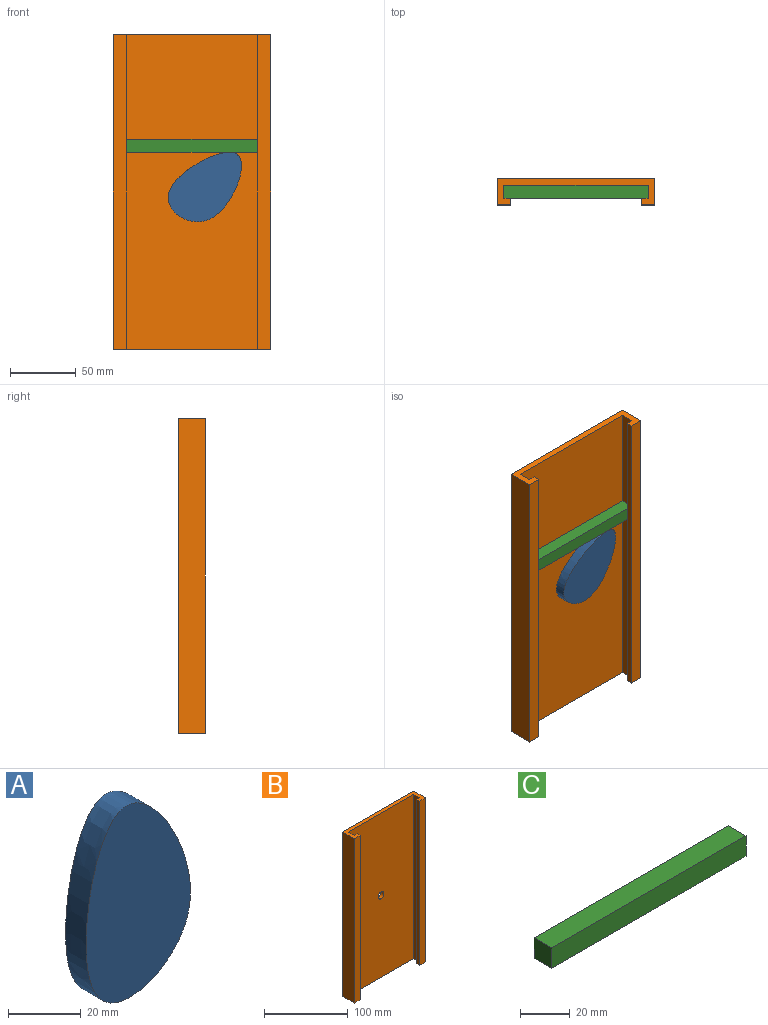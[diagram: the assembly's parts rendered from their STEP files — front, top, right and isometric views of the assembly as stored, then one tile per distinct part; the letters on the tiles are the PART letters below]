
ASSEMBLY  parts=3 mates=2
PART A: 5 faces, bbox 45.8x15x68.5 mm
  f0: plane 10x10mm, normal (0,1,0), area 78.5mm2, adj f1
  f1: cylinder r=5mm len=10mm, axis (0,-1,0), area 219.9mm2, adj f0,f4
  f2: extruded ~65.05x40.46mm, area 1344.3mm2, adj f3,f4
  f3: plane 68.49x45.81mm, normal (0,-1,0), area 2019.8mm2, adj f2
  f4: plane 68.49x45.81mm, normal (0,1,0), area 1941.3mm2, adj f1,f2
PART B: 15 faces, bbox 120x20x240 mm
  f0: plane 240x5mm, normal (1,0,0), area 1200mm2, adj f1,f3,f8,f13
  f1: plane 120x20mm, normal (0,0,-1), area 800mm2, adj f0,f2,f4,f5,f6,f7,f8,f9
  f2: plane 240x5mm, normal (-1,0,0), area 1200mm2, adj f1,f3,f6,f11
  f3: plane 120x20mm, normal (0,0,1), area 800mm2, adj f0,f2,f4,f5,f6,f7,f8,f9
  f4: plane 240x110mm, normal (0,-1,0), area 26321.5mm2, adj f1,f3,f5,f7,f14
  f5: plane 240x10mm, normal (-1,0,0), area 2400mm2, adj f1,f3,f4,f6
  f6: plane 240x5mm, normal (0,1,0), area 1200mm2, adj f1,f2,f3,f5
  f7: plane 240x10mm, normal (1,0,0), area 2400mm2, adj f1,f3,f4,f8
  f8: plane 240x5mm, normal (0,1,0), area 1200mm2, adj f0,f1,f3,f7
  f9: plane 240x120mm, normal (0,1,0), area 28721.5mm2, adj f1,f3,f10,f12,f14
  f10: plane 240x20mm, normal (1,0,0), area 4800mm2, adj f1,f3,f9,f11
  f11: plane 240x10mm, normal (0,-1,0), area 2400mm2, adj f1,f2,f3,f10
  f12: plane 240x20mm, normal (-1,0,0), area 4800mm2, adj f1,f3,f9,f13
  f13: plane 240x10mm, normal (0,-1,0), area 2400mm2, adj f0,f1,f3,f12
  f14: cylinder r=5mm len=10mm, axis (0,-1,0), area 157.1mm2, adj f4,f9
PART C: 6 faces, bbox 110x10x10 mm
  f0: plane 10x10mm, normal (1,0,0), area 100mm2, adj f1,f2,f4,f5
  f1: plane 110x10mm, normal (0,0,1), area 1100mm2, adj f0,f3,f4,f5
  f2: plane 110x10mm, normal (0,0,-1), area 1100mm2, adj f0,f3,f4,f5
  f3: plane 10x10mm, normal (-1,0,0), area 100mm2, adj f1,f2,f4,f5
  f4: plane 110x10mm, normal (0,1,0), area 1100mm2, adj f0,f1,f2,f3
  f5: plane 110x10mm, normal (0,-1,0), area 1100mm2, adj f0,f1,f2,f3
PLACE A rot(axis=(0,1,0),52.1deg) t=(-73.68,0,94.72)mm
PLACE B at identity fixed
PLACE C rot(axis=(0.08,0.04,1),0deg) t=(0,0,-79.76)mm
MATE slider C.f1 <-> B.f3  axis (0,0,1) through (-55,2,40.24)mm
MATE revolute B.f14 <-> A.f1  axis (0,1,0) through (0,7,0)mm
